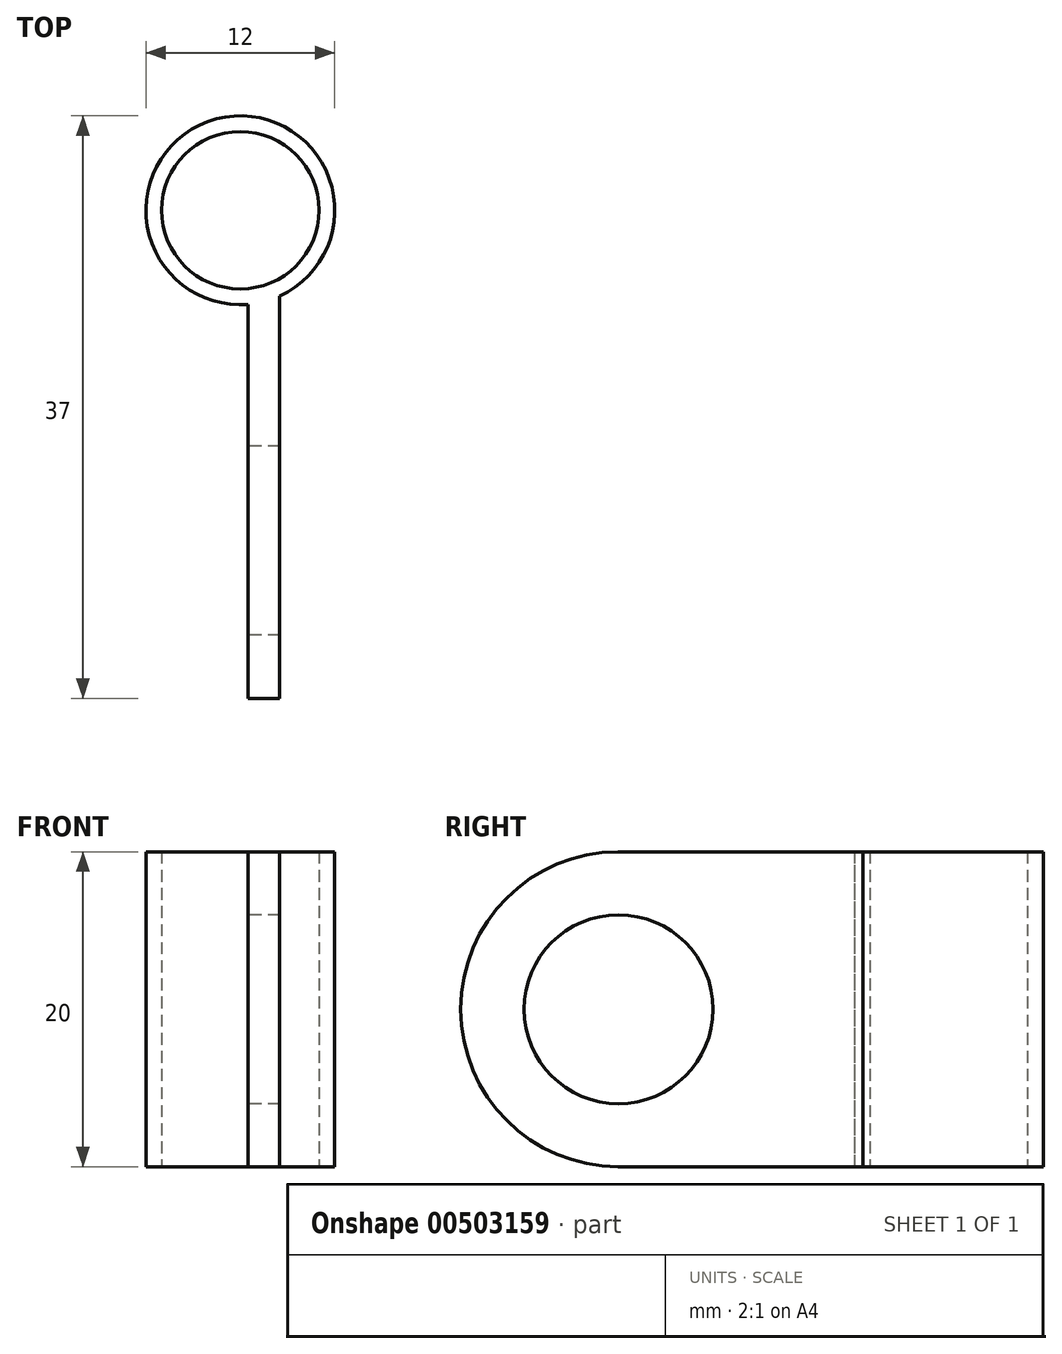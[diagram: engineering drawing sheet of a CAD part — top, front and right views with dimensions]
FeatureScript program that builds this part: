
annotation { "Feature Type Name" : "Feature", "Feature Type Description" : "" }
export const myFeature = defineFeature(function(context is Context, id is Id, definition is map)
    precondition{}
    {
        {
            var Q0;
            Q0=qCreatedBy(makeId("Top.planeOp"),FACE);
            var sketch = newSketch(context, id + "F0", { "sketchPlane" : qUnion([Q0])});
            skCircle(sketch, "E0", {"center": v(0, 0) * mm, "radius": 5 * mm});
            skCircle(sketch, "E1", {"center": v(0, 0) * mm, "radius": 6 * mm});
            skSolve(sketch);
        }
        {
            var Q0;
            Q0=makeQuery(id+"F0.imprint","IMPRINT",FACE,{"disambiguationData":[TD([[makeQuery(id+"F0.imprint","IMPRINT",EDGE,{"derivedFrom":sQuery(id+"F0.wireOp",EDGE,"E0")}),-1.0]])]});
            extrude(context, id + "F1", {"entities" : qUnion([Q0]), "depth" : 20 * mm});
        }
        {
            var Q0;
            Q0=makeQuery(id+"F1.opExtrude","CAP_FACE",FACE,{"disambiguationData":[OSD([sQuery(id+"F0.wireOp",EDGE,"E0"),sQuery(id+"F0.wireOp",EDGE,"E1")])],"isStart":false});
            var sketch = newSketch(context, id + "F2", { "sketchPlane" : qUnion([Q0])});
            skLineSegment(sketch, "E2", {"start": v(0, 0) * mm, "end": v(0, -6) * mm, "construction": true});
            skLineSegment(sketch, "E3", {"start": v(0, -6) * mm, "end": v(0.5, -6) * mm, "construction": true});
            skLineSegment(sketch, "E4.top", {"start": v(0.5, -31) * mm, "end": v(2.5, -31) * mm});
            skLineSegment(sketch, "E4.left", {"start": v(0.5, -6) * mm, "end": v(0.5, -31) * mm});
            skLineSegment(sketch, "E4.right", {"start": v(2.5, -6) * mm, "end": v(2.5, -31) * mm});
            skLineSegment(sketch, "E5", {"start": v(2.5, -6) * mm, "end": v(2.5, -5.45) * mm});
            skLineSegment(sketch, "E6", {"start": v(0.5, -6) * mm, "end": v(0.5, -5.97) * mm});
            skSolve(sketch);
        }
        {
            var Q0;
            Q0=makeQuery(id+"F2.imprint","IMPRINT",FACE,{"disambiguationData":[TD([[makeQuery(id+"F2.imprint","IMPRINT",EDGE,{"derivedFrom":sQuery(id+"F2.wireOp",EDGE,"E4.top")}),1.0]])]});
            extrude(context, id + "F3", {"entities" : qUnion([Q0]), "operationType" : NewBodyOperationType.ADD, "oppositeDirection" : true, "depth" : 20 * mm});
        }
        {
            var Q0;
            Q0=makeQuery(id+"F3.opExtrude","SWEPT_FACE",FACE,{"disambiguationData":[OSD([sQuery(id+"F2.wireOp",EDGE,"E4.left"),sQuery(id+"F2.wireOp",EDGE,"E6")])]});
            var sketch = newSketch(context, id + "F4", { "sketchPlane" : qUnion([Q0])});
            skLineSegment(sketch, "E7", {"start": v(5.98, 10) * mm, "end": v(20.98, 10) * mm, "construction": true});
            skCircle(sketch, "E8", {"center": v(20.98, 10) * mm, "radius": 6 * mm});
            skSolve(sketch);
        }
        {
            var Q0;
            Q0=makeQuery(id+"F4.imprint","IMPRINT",FACE,{"disambiguationData":[TD([[makeQuery(id+"F4.imprint","IMPRINT",EDGE,{"derivedFrom":sQuery(id+"F4.wireOp",EDGE,"E8")}),1.0]])]});
            extrude(context, id + "F5", {"entities" : qUnion([Q0]), "operationType" : NewBodyOperationType.REMOVE, "endBound" : BoundingType.THROUGH_ALL, "oppositeDirection" : true, "depth" : 25 * mm});
        }
        {
            var Q0;
            Q0=makeQuery(id+"F3.opExtrude","CAP_EDGE",EDGE,{"disambiguationData":[OSD([sQuery(id+"F2.wireOp",EDGE,"E4.top")])],"isStart":true});
            var Q1;
            Q1=makeQuery(id+"F3.opExtrude","CAP_EDGE",EDGE,{"disambiguationData":[OSD([sQuery(id+"F2.wireOp",EDGE,"E4.top")])],"isStart":false});
            fillet(context, id + "F6", {"entities" : qUnion([Q0, Q1]), "radius" : 10 * mm, "tangentPropagation" : true, "allowEdgeOverflow" : false});
        }
    });
